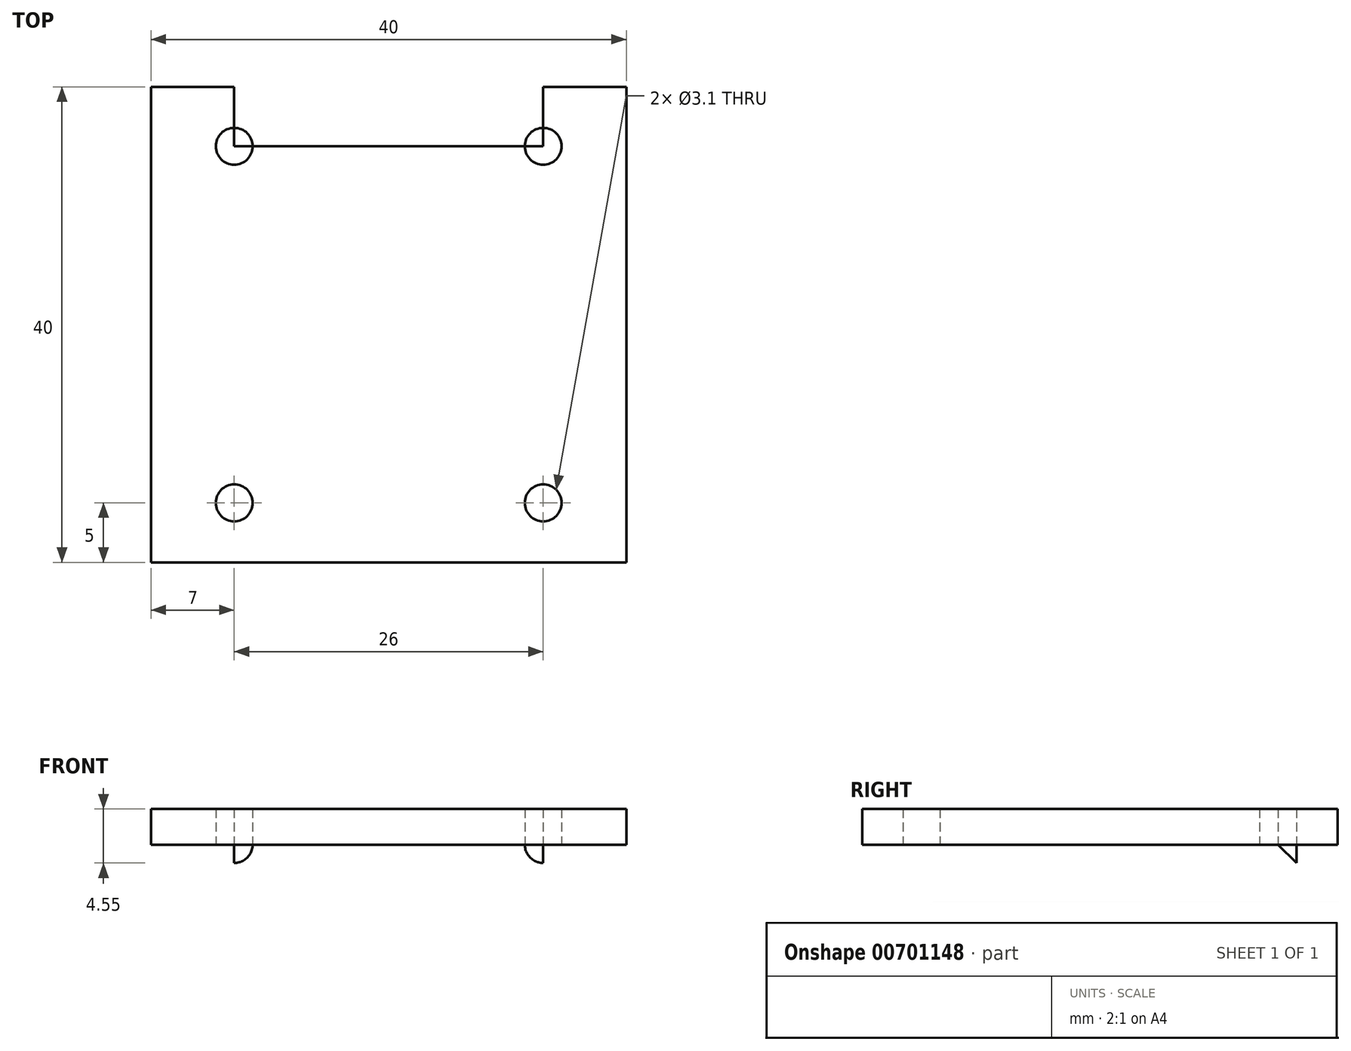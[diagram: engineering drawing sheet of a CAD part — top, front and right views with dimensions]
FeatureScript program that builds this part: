
annotation { "Feature Type Name" : "Feature", "Feature Type Description" : "" }
export const myFeature = defineFeature(function(context is Context, id is Id, definition is map)
    precondition{}
    {
        {
            var Q0;
            Q0=qCreatedBy(makeId("Top.planeOp"),FACE);
            var sketch = newSketch(context, id + "F0", { "sketchPlane" : qUnion([Q0])});
            skLineSegment(sketch, "E0.bottom", {"start": v(13, -15) * mm, "end": v(-13, -15) * mm});
            skLineSegment(sketch, "E0.top", {"start": v(13, 15) * mm, "end": v(-13, 15) * mm});
            skLineSegment(sketch, "E0.left", {"start": v(13, -15) * mm, "end": v(13, 15) * mm});
            skLineSegment(sketch, "E0.right", {"start": v(-13, -15) * mm, "end": v(-13, 15) * mm});
            skPoint(sketch, "E0.middle", {"position": v(0, 0) * mm});
            skLineSegment(sketch, "E1.bottom", {"start": v(20, -20) * mm, "end": v(-20, -20) * mm});
            skLineSegment(sketch, "E1.top", {"start": v(20, 20) * mm, "end": v(-20, 20) * mm});
            skLineSegment(sketch, "E1.left", {"start": v(20, -20) * mm, "end": v(20, 20) * mm});
            skLineSegment(sketch, "E1.right", {"start": v(-20, -20) * mm, "end": v(-20, 20) * mm});
            skLineSegment(sketch, "E2.bottom", {"start": v(-20, 20) * mm, "end": v(20, 20) * mm});
            skLineSegment(sketch, "E2.top", {"start": v(-20, 30) * mm, "end": v(20, 30) * mm});
            skLineSegment(sketch, "E2.left", {"start": v(-20, 20) * mm, "end": v(-20, 30) * mm});
            skLineSegment(sketch, "E2.right", {"start": v(20, 20) * mm, "end": v(20, 30) * mm});
            skLineSegment(sketch, "E3.bottom", {"start": v(-20, 30) * mm, "end": v(-15, 30) * mm});
            skLineSegment(sketch, "E3.top", {"start": v(-20, 25) * mm, "end": v(-15, 25) * mm});
            skLineSegment(sketch, "E3.left", {"start": v(-20, 30) * mm, "end": v(-20, 25) * mm});
            skLineSegment(sketch, "E3.right", {"start": v(-15, 30) * mm, "end": v(-15, 25) * mm});
            skLineSegment(sketch, "E4.bottom", {"start": v(-15, 30) * mm, "end": v(15, 30) * mm});
            skLineSegment(sketch, "E4.top", {"start": v(-15, 25) * mm, "end": v(15, 25) * mm});
            skLineSegment(sketch, "E4.right", {"start": v(15, 30) * mm, "end": v(15, 25) * mm});
            skCircle(sketch, "E5", {"center": v(-15, 25) * mm, "radius": 1.55 * mm});
            skCircle(sketch, "E6", {"center": v(15, 25) * mm, "radius": 1.55 * mm});
            skCircle(sketch, "E7", {"center": v(-13, 15) * mm, "radius": 1.55 * mm});
            skCircle(sketch, "E8", {"center": v(13, 15) * mm, "radius": 1.55 * mm});
            skCircle(sketch, "E9", {"center": v(13, -15) * mm, "radius": 1.55 * mm});
            skCircle(sketch, "E10", {"center": v(-13, -15) * mm, "radius": 1.55 * mm});
            skLineSegment(sketch, "E11.top", {"start": v(13, 20) * mm, "end": v(-13, 20) * mm});
            skLineSegment(sketch, "E11.left", {"start": v(13, 15) * mm, "end": v(13, 20) * mm});
            skLineSegment(sketch, "E11.right", {"start": v(-13, 15) * mm, "end": v(-13, 20) * mm});
            skLineSegment(sketch, "E12.bottom", {"start": v(13, 15) * mm, "end": v(8, 15) * mm});
            skLineSegment(sketch, "E12.top", {"start": v(13, 20) * mm, "end": v(8, 20) * mm});
            skLineSegment(sketch, "E12.right", {"start": v(8, 15) * mm, "end": v(8, 20) * mm});
            skLineSegment(sketch, "E13.bottom", {"start": v(-13, 20) * mm, "end": v(-8, 20) * mm});
            skLineSegment(sketch, "E13.top", {"start": v(-13, 15) * mm, "end": v(-8, 15) * mm});
            skLineSegment(sketch, "E13.left", {"start": v(-13, 20) * mm, "end": v(-13, 15) * mm});
            skLineSegment(sketch, "E13.right", {"start": v(-8, 20) * mm, "end": v(-8, 15) * mm});
            skSolve(sketch);
        }
        {
            var Q0;
            {var subQ5=sQuery(id+"F0.wireOp",EDGE,"E9");var subQ10=sQuery(id+"F0.wireOp",EDGE,"E0.bottom");var subQ11=makeQuery(id+"F0.imprint","INTERSECT",VERTEX,{"derivedFrom":[subQ10,subQ5]});Q0=makeQuery(id+"F0.imprint","IMPRINT",FACE,{"disambiguationData":[TD([[makeQuery(id+"F0.imprint","IMPRINT",EDGE,{"disambiguationData":[TD([[subQ11,-1.0]])],"derivedFrom":subQ10}),-1.0]])]});}
            var Q1;
            Q1=makeQuery(id+"F0.imprint","IMPRINT",FACE,{"disambiguationData":[TD([[makeQuery(id+"F0.imprint","IMPRINT",EDGE,{"derivedFrom":sQuery(id+"F0.wireOp",EDGE,"E1.bottom")}),-1.0]])]});
            var Q2;
            Q2=makeQuery(id+"F0.imprint","IMPRINT",FACE,{"disambiguationData":[TD([[makeQuery(id+"F0.imprint","IMPRINT",EDGE,{"derivedFrom":sQuery(id+"F0.wireOp",EDGE,"E2.bottom")}),1.0]])]});
            var Q3;
            {var subQ1=sQuery(id+"F0.wireOp",EDGE,"E4.bottom");Q3=makeQuery(id+"F0.imprint","IMPRINT",FACE,{"disambiguationData":[TD([[makeQuery(id+"F0.imprint","IMPRINT",EDGE,{"derivedFrom":subQ1}),-1.0]])]});}
            var Q4;
            {var subQ1=sQuery(id+"F0.wireOp",EDGE,"E3.bottom");Q4=makeQuery(id+"F0.imprint","IMPRINT",FACE,{"disambiguationData":[TD([[makeQuery(id+"F0.imprint","IMPRINT",EDGE,{"derivedFrom":subQ1}),-1.0]])]});}
            var Q5;
            Q5=makeQuery(id+"F0.imprint","IMPRINT",FACE,{"disambiguationData":[TD([[makeQuery(id+"F0.imprint","IMPRINT",EDGE,{"derivedFrom":sQuery(id+"F0.wireOp",EDGE,"E0.top")}),-1.0]])]});
            var Q6;
            {var subQ1=sQuery(id+"F0.wireOp",EDGE,"E12.top");Q6=makeQuery(id+"F0.imprint","IMPRINT",FACE,{"disambiguationData":[TD([[makeQuery(id+"F0.imprint","IMPRINT",EDGE,{"derivedFrom":subQ1}),1.0]])]});}
            var Q7;
            {var subQ1=sQuery(id+"F0.wireOp",EDGE,"E13.bottom");Q7=makeQuery(id+"F0.imprint","IMPRINT",FACE,{"disambiguationData":[TD([[makeQuery(id+"F0.imprint","IMPRINT",EDGE,{"derivedFrom":subQ1}),-1.0]])]});}
            extrude(context, id + "F1", {"entities" : qUnion([Q0, Q1, Q2, Q3, Q4, Q5, Q6, Q7]), "depth" : 3 * mm, "offsetDistance" : 25 * mm});
        }
        {
            var Q0;
            Q0=makeQuery(id+"F0.imprint","IMPRINT",FACE,{"disambiguationData":[TD([[makeQuery(id+"F0.imprint","IMPRINT",EDGE,{"derivedFrom":sQuery(id+"F0.wireOp",EDGE,"E0.top")}),-1.0]])]});
            extrude(context, id + "F2", {"entities" : qUnion([Q0]), "operationType" : NewBodyOperationType.ADD, "oppositeDirection" : true, "depth" : 5 * mm, "offsetDistance" : 25 * mm});
        }
        {
            var Q0;
            Q0=makeQuery(id+"F2.opExtrude","CAP_EDGE",EDGE,{"disambiguationData":[OSD([sQuery(id+"F0.wireOp",EDGE,"E0.top")])],"isStart":false});
            chamfer(context, id + "F3", {"entities" : qUnion([Q0]), "width" : 5 * mm, "tangentPropagation" : true});
        }
    });
